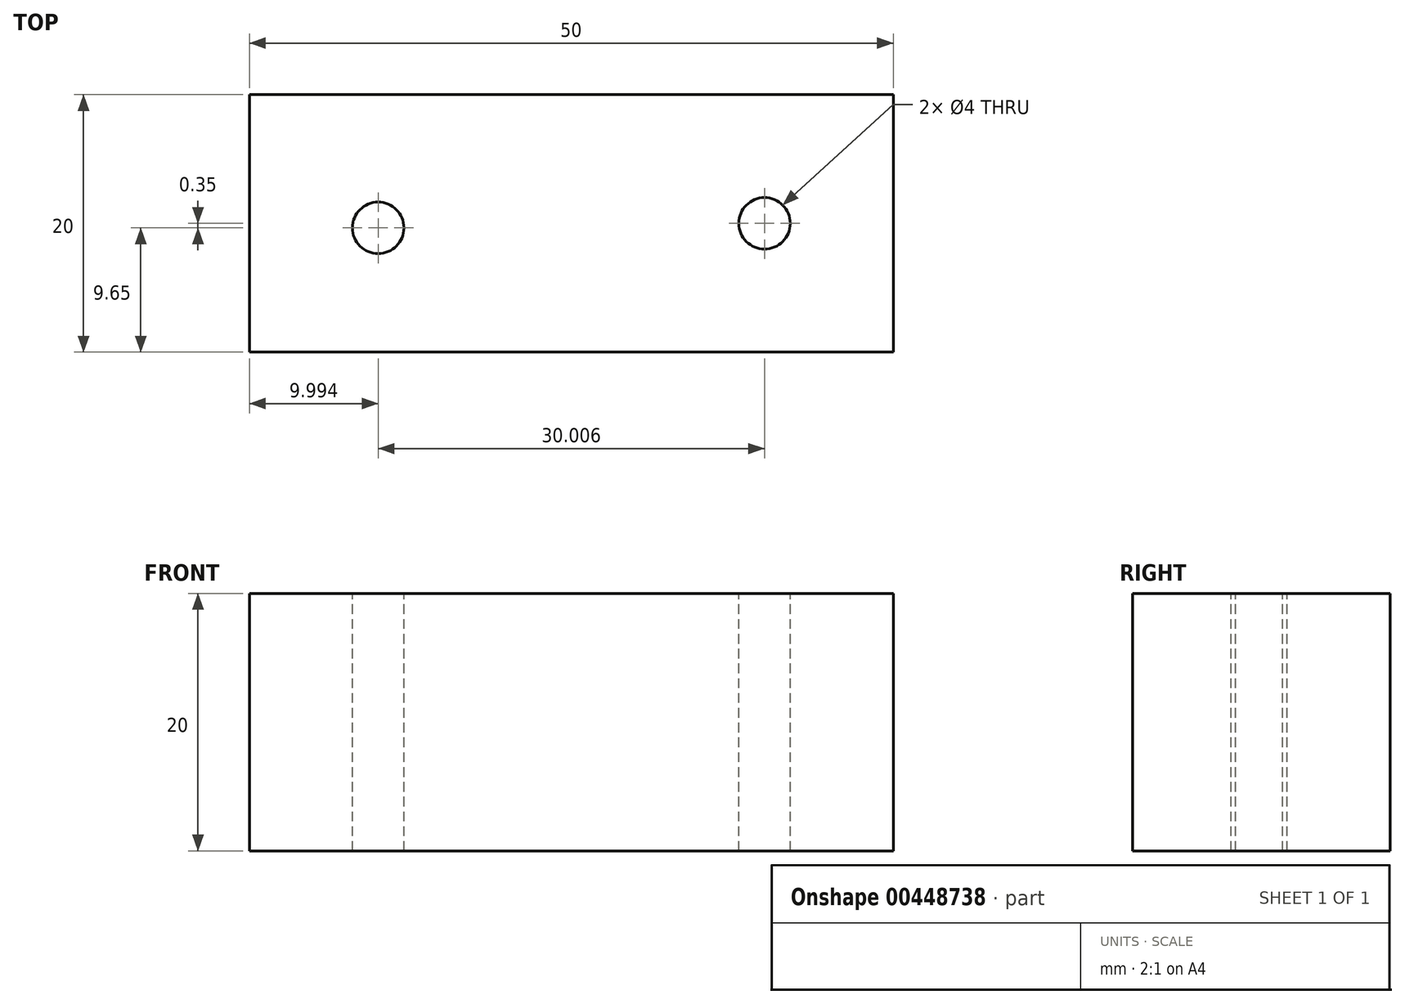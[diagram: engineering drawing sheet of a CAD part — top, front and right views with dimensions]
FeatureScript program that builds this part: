
annotation { "Feature Type Name" : "Feature", "Feature Type Description" : "" }
export const myFeature = defineFeature(function(context is Context, id is Id, definition is map)
    precondition{}
    {
        {
            var Q0;
            Q0=qCreatedBy(makeId("Top.planeOp"),FACE);
            var sketch = newSketch(context, id + "F0", { "sketchPlane" : qUnion([Q0])});
            skLineSegment(sketch, "E0.bottom", {"start": v(-25, 10) * mm, "end": v(25, 10) * mm});
            skLineSegment(sketch, "E0.top", {"start": v(-25, -10) * mm, "end": v(25, -10) * mm});
            skLineSegment(sketch, "E0.left", {"start": v(-25, 10) * mm, "end": v(-25, -10) * mm});
            skLineSegment(sketch, "E0.right", {"start": v(25, 10) * mm, "end": v(25, -10) * mm});
            skPoint(sketch, "E0.middle", {"position": v(0, 0) * mm});
            skSolve(sketch);
        }
        {
            var Q0;
            Q0 = qSketchRegion(id + "F0", true);
            extrude(context, id + "F1", {"entities" : qUnion([Q0]), "depth" : 20 * mm});
        }
        {
            var Q0;
            Q0=makeQuery(id+"F1.opExtrude","CAP_FACE",FACE,{"disambiguationData":[OSD([sQuery(id+"F0.wireOp",EDGE,"E0.bottom"),sQuery(id+"F0.wireOp",EDGE,"E0.top"),sQuery(id+"F0.wireOp",EDGE,"E0.left"),sQuery(id+"F0.wireOp",EDGE,"E0.right")])],"isStart":false});
            var sketch = newSketch(context, id + "F2", { "sketchPlane" : qUnion([Q0])});
            skLineSegment(sketch, "E1", {"start": v(25, 0) * mm, "end": v(15, 0) * mm});
            skPoint(sketch, "E1.endSnap0", {"position": v(25, 0) * mm});
            skLineSegment(sketch, "E2", {"start": v(-25, 0) * mm, "end": v(-15, -0.35) * mm});
            skCircle(sketch, "E3", {"center": v(-15, -0.35) * mm, "radius": 2 * mm});
            skCircle(sketch, "E4", {"center": v(15, 0) * mm, "radius": 2 * mm});
            skSolve(sketch);
        }
        {
            var Q0;
            Q0=makeQuery(id+"F2.imprint","IMPRINT",FACE,{"disambiguationData":[TD([[makeQuery(id+"F2.imprint","IMPRINT",EDGE,{"derivedFrom":sQuery(id+"F2.wireOp",EDGE,"E3")}),1.0]])]});
            var Q1;
            Q1=makeQuery(id+"F2.imprint","IMPRINT",FACE,{"disambiguationData":[TD([[makeQuery(id+"F2.imprint","IMPRINT",EDGE,{"derivedFrom":sQuery(id+"F2.wireOp",EDGE,"E4")}),1.0]])]});
            extrude(context, id + "F3", {"entities" : qUnion([Q0, Q1]), "operationType" : NewBodyOperationType.REMOVE, "oppositeDirection" : true, "depth" : 25 * mm});
        }
    });
